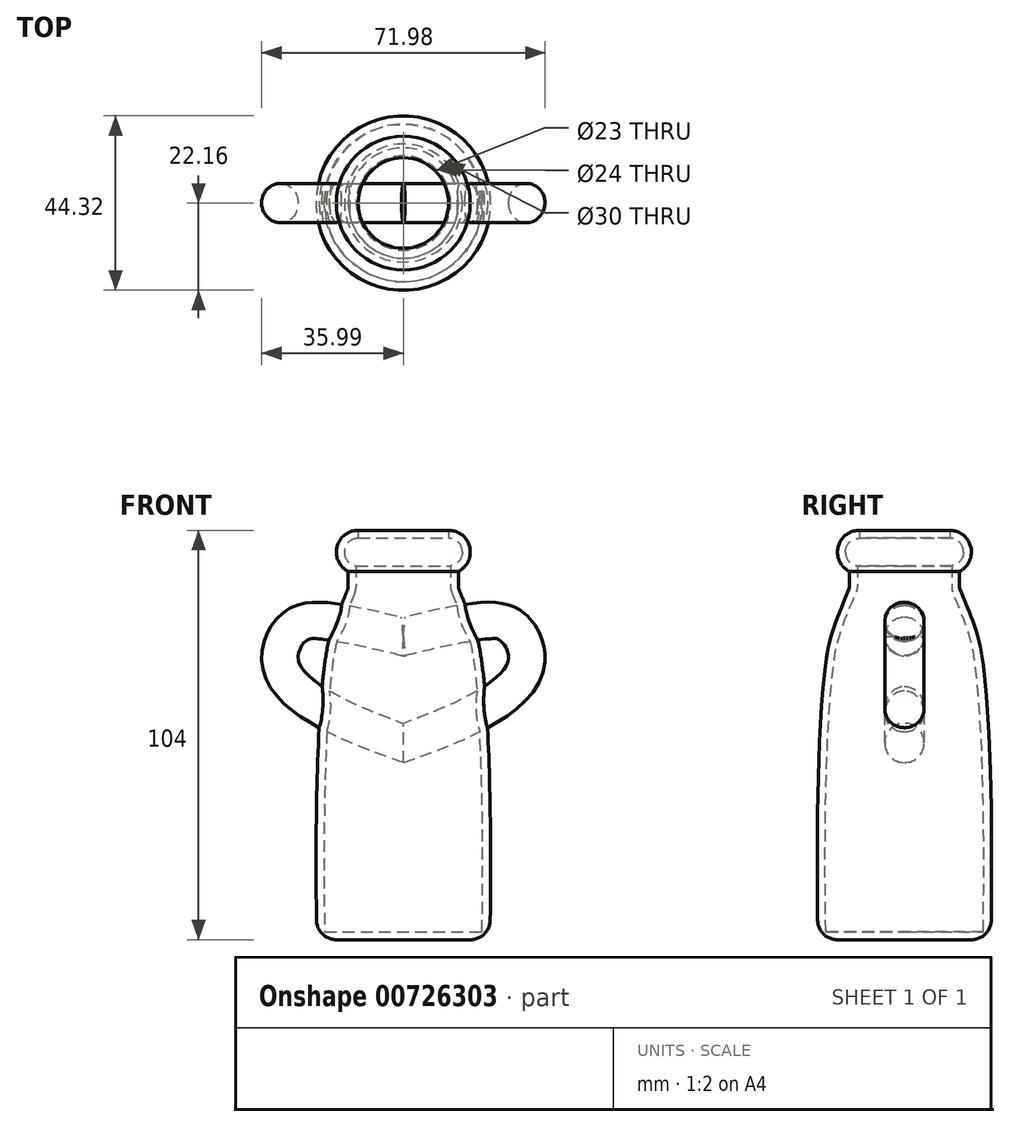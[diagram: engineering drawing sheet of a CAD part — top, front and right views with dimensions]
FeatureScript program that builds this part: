
annotation { "Feature Type Name" : "Feature", "Feature Type Description" : "" }
export const myFeature = defineFeature(function(context is Context, id is Id, definition is map)
    precondition{}
    {
        {
            var Q0;
            Q0=qCreatedBy(makeId("Front.planeOp"),FACE);
            var sketch = newSketch(context, id + "F0", { "sketchPlane" : qUnion([Q0])});
            skLineSegment(sketch, "E0", {"start": v(20, 0) * mm, "end": v(0, 0) * mm});
            skLineSegment(sketch, "E1", {"start": v(0, 0) * mm, "end": v(0, 100) * mm});
            skLineSegment(sketch, "E2", {"start": v(0, 100) * mm, "end": v(15, 100) * mm});
            skLineSegment(sketch, "E3", {"start": v(15, 100) * mm, "end": v(15, 93) * mm});
            skLineSegment(sketch, "E4", {"start": v(15, 93) * mm, "end": v(12, 93) * mm});
            skLineSegment(sketch, "E5", {"start": v(12, 93) * mm, "end": v(12, 87) * mm});
            skFitSpline(sketch, "E6", {"points": [v(12, 87) * mm, v(17.58, 70.58) * mm, v(20, 0) * mm], "startDerivative": vector(28.33, -72.49) * mm, "endDerivative": vector(-2.41, -133.97) * mm});
            skPoint(sketch, "E7.endSnap0", {"position": v(15, 96.5) * mm});
            skSolve(sketch);
        }
        {
            var Q0;
            Q0=makeQuery(id+"F0.imprint","IMPRINT",FACE,{"disambiguationData":[TD([[makeQuery(id+"F0.imprint","IMPRINT",EDGE,{"derivedFrom":sQuery(id+"F0.wireOp",EDGE,"E0")}),-1.0]])]});
            var Q1;
            Q1=sQuery(id+"F0.wireOp",EDGE,"E1");
            revolve(context, id + "F1", {"surfaceOperationType" : NewSurfaceOperationType.NEW, "entities" : qUnion([Q0]), "axis" : qUnion([Q1]), "revolveType" : RevolveType.FULL});
        }
        {
            var Q0;
            Q0=makeQuery(id+"F1.opRevolve","SWEPT_EDGE",EDGE,{"disambiguationData":[OSD([sQuery(id+"F0.wireOp",EDGE,"E2"),sQuery(id+"F0.wireOp",EDGE,"E3")])]});
            var Q1;
            Q1=makeQuery(id+"F1.opRevolve","SWEPT_EDGE",EDGE,{"disambiguationData":[OSD([sQuery(id+"F0.wireOp",EDGE,"E3"),sQuery(id+"F0.wireOp",EDGE,"E4")])]});
            var Q2;
            Q2=makeQuery(id+"F1.opRevolve","SWEPT_EDGE",EDGE,{"disambiguationData":[OSD([sQuery(id+"F0.wireOp",EDGE,"E5"),sQuery(id+"F0.wireOp",EDGE,"E6")])]});
            fillet(context, id + "F2", {"entities" : qUnion([Q0, Q1, Q2]), "radius" : 3.5 * mm, "tangentPropagation" : true, "allowEdgeOverflow" : false});
        }
        {
            var Q0;
            Q0=makeQuery(id+"F1.opRevolve","SWEPT_FACE",FACE,{"disambiguationData":[OSD([sQuery(id+"F0.wireOp",EDGE,"E2")])]});
            shell(context, id + "F3", {"entities" : qUnion([Q0]), "thickness" : 2 * mm, "oppositeDirection" : true});
        }
        {
            var Q0;
            Q0=qCreatedBy(makeId("Front.planeOp"),FACE);
            var sketch = newSketch(context, id + "F4", { "sketchPlane" : qUnion([Q0])});
            skFitSpline(sketch, "E8", {"points": [v(0, 75) * mm, v(17.02, 78.59) * mm, v(27.6, 77.27) * mm, v(30.7, 66.72) * mm, v(0, 48) * mm], "startDerivative": vector(69.57, 17.3) * mm, "endDerivative": vector(-131.5, -45.95) * mm});
            skSolve(sketch);
        }
        {
            var Q0;
            Q0=qCreatedBy(makeId("Right.planeOp"),FACE);
            var sketch = newSketch(context, id + "F5", { "sketchPlane" : qUnion([Q0])});
            skCircle(sketch, "E9", {"center": v(0, 48) * mm, "radius": 5 * mm});
            skSolve(sketch);
        }
        {
            var Q0;
            Q0 = qSketchRegion(id + "F5", true);
            var Q1;
            Q1=sQuery(id+"F4.wireOp",EDGE,"E8");
            sweep(context, id + "F6", {"operationType" : NewBodyOperationType.ADD, "profiles" : qUnion([Q0]), "path" : qUnion([Q1])});
        }
        {
            var Q0;
            Q0=makeQuery(id+"F1.opRevolve","SWEPT_BODY",BODY,{"disambiguationData":[OSD([sQuery(id+"F0.wireOp",EDGE,"E0"),sQuery(id+"F0.wireOp",EDGE,"E1"),sQuery(id+"F0.wireOp",EDGE,"E2"),sQuery(id+"F0.wireOp",EDGE,"E3"),sQuery(id+"F0.wireOp",EDGE,"E4"),sQuery(id+"F0.wireOp",EDGE,"E5"),sQuery(id+"F0.wireOp",EDGE,"E6")])]});
            var Q1;
            Q1=qCreatedBy(makeId("Right.planeOp"),FACE);
            mirror(context, id + "F7", {"operationType" : NewBodyOperationType.ADD, "entities" : qUnion([Q0]), "mirrorPlane" : qUnion([Q1])});
        }
        {
            var Q0;
            Q0=makeQuery(id+"F1.opRevolve","SWEPT_EDGE",EDGE,{"disambiguationData":[OSD([sQuery(id+"F0.wireOp",EDGE,"E0"),sQuery(id+"F0.wireOp",EDGE,"E6")])]});
            fillet(context, id + "F8", {"entities" : qUnion([Q0]), "radius" : 5 * mm, "tangentPropagation" : true, "allowEdgeOverflow" : false});
        }
    });
